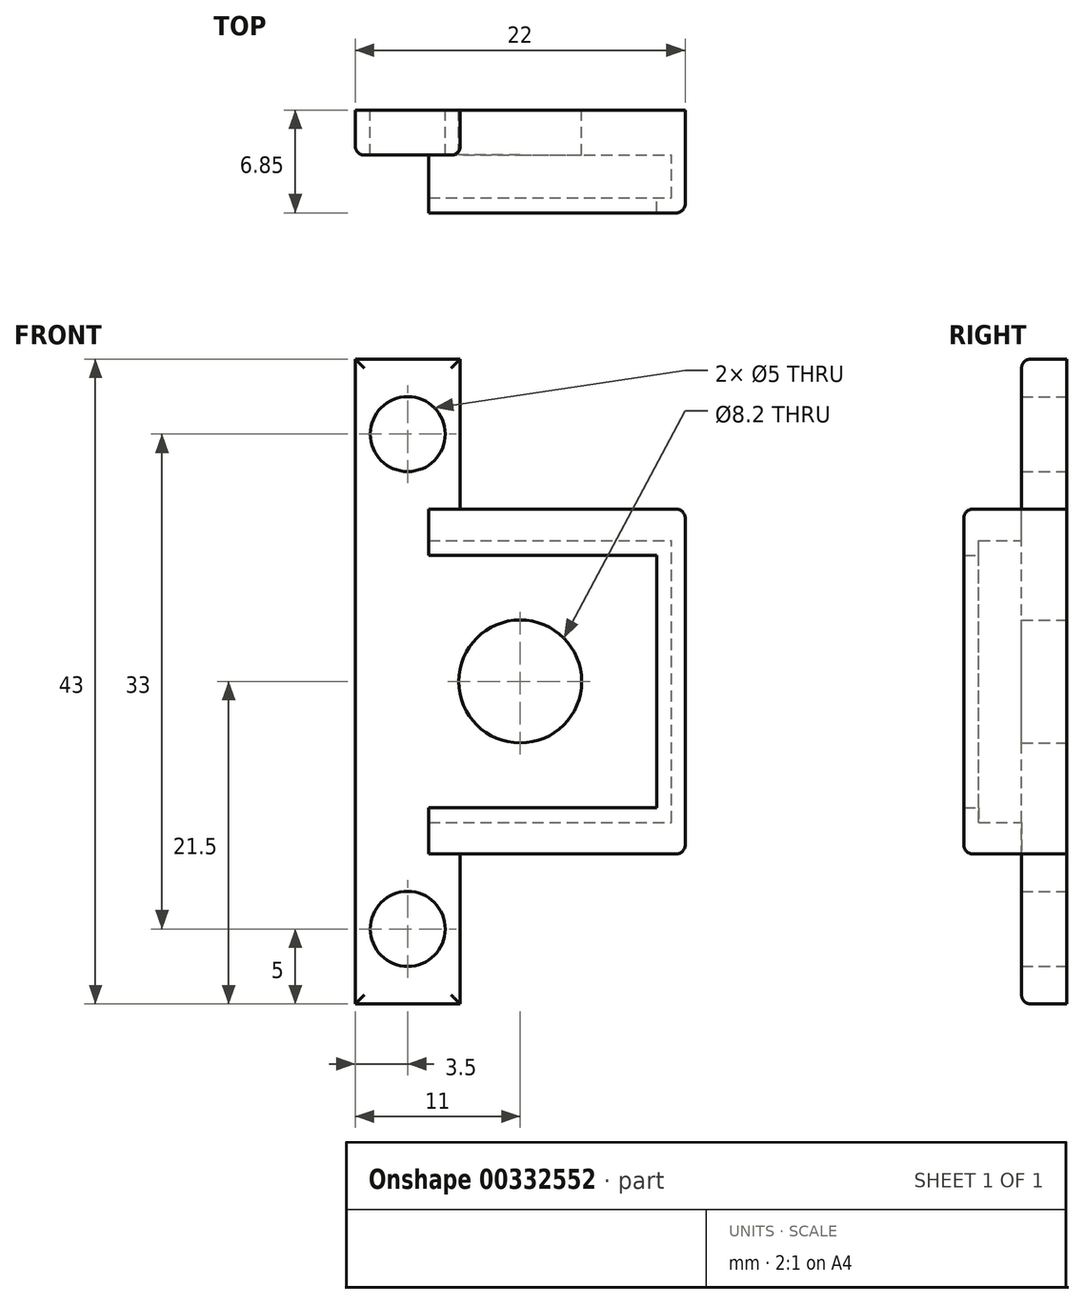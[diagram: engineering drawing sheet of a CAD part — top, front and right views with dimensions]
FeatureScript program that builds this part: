
annotation { "Feature Type Name" : "Feature", "Feature Type Description" : "" }
export const myFeature = defineFeature(function(context is Context, id is Id, definition is map)
    precondition{}
    {
        {
            var Q0;
            Q0=qCreatedBy(makeId("Front.planeOp"),FACE);
            var sketch = newSketch(context, id + "F0", { "sketchPlane" : qUnion([Q0])});
            skLineSegment(sketch, "E0.bottom", {"start": v(0, 0) * mm, "end": v(22, 0) * mm});
            skLineSegment(sketch, "E0.top", {"start": v(0, 23) * mm, "end": v(22, 23) * mm});
            skLineSegment(sketch, "E0.left", {"start": v(0, 0) * mm, "end": v(0, 23) * mm});
            skLineSegment(sketch, "E0.right", {"start": v(22, 0) * mm, "end": v(22, 23) * mm});
            skLineSegment(sketch, "E1.bottom", {"start": v(21.1, 20.9) * mm, "end": v(0.9, 20.9) * mm});
            skLineSegment(sketch, "E1.top", {"start": v(21.1, 2.1) * mm, "end": v(0.9, 2.1) * mm});
            skLineSegment(sketch, "E1.left", {"start": v(21.1, 20.9) * mm, "end": v(21.1, 2.1) * mm});
            skLineSegment(sketch, "E1.right", {"start": v(0.9, 20.9) * mm, "end": v(0.9, 2.1) * mm});
            skPoint(sketch, "E2", {"position": v(4.9, 20.9) * mm});
            skPoint(sketch, "E3", {"position": v(4.9, 2.1) * mm});
            skPoint(sketch, "E4", {"position": v(22, 1.5) * mm});
            skPoint(sketch, "E5", {"position": v(22, 21.5) * mm});
            skPoint(sketch, "E6", {"position": v(0, 1.5) * mm});
            skLineSegment(sketch, "E7.bottom", {"start": v(22, 0) * mm, "end": v(15, 0) * mm});
            skLineSegment(sketch, "E7.top", {"start": v(22, -10) * mm, "end": v(15, -10) * mm});
            skLineSegment(sketch, "E7.left", {"start": v(22, 0) * mm, "end": v(22, -10) * mm});
            skLineSegment(sketch, "E7.right", {"start": v(15, 0) * mm, "end": v(15, -10) * mm});
            skLineSegment(sketch, "E8.bottom", {"start": v(0, 0) * mm, "end": v(7, 0) * mm});
            skLineSegment(sketch, "E8.top", {"start": v(0, -10) * mm, "end": v(7, -10) * mm});
            skLineSegment(sketch, "E8.left", {"start": v(0, 0) * mm, "end": v(0, -10) * mm});
            skLineSegment(sketch, "E8.right", {"start": v(7, 0) * mm, "end": v(7, -10) * mm});
            skLineSegment(sketch, "E9.bottom", {"start": v(0, 23) * mm, "end": v(7, 23) * mm});
            skLineSegment(sketch, "E9.top", {"start": v(0, 33) * mm, "end": v(7, 33) * mm});
            skLineSegment(sketch, "E9.left", {"start": v(0, 23) * mm, "end": v(0, 33) * mm});
            skLineSegment(sketch, "E9.right", {"start": v(7, 23) * mm, "end": v(7, 33) * mm});
            skLineSegment(sketch, "E10.bottom", {"start": v(22, 23) * mm, "end": v(15, 23) * mm});
            skLineSegment(sketch, "E10.top", {"start": v(22, 33) * mm, "end": v(15, 33) * mm});
            skLineSegment(sketch, "E10.left", {"start": v(22, 23) * mm, "end": v(22, 33) * mm});
            skLineSegment(sketch, "E10.right", {"start": v(15, 23) * mm, "end": v(15, 33) * mm});
            skPoint(sketch, "E11", {"position": v(11, 11.5) * mm});
            skLineSegment(sketch, "E12", {"start": v(13.1, 11.9) * mm, "end": v(8.66, 7.89) * mm});
            skPoint(sketch, "E13", {"position": v(3.5, -5) * mm});
            skLineSegment(sketch, "E14", {"start": v(4.03, -4.24) * mm, "end": v(2.85, -5.92) * mm});
            skPoint(sketch, "E15", {"position": v(3.5, 28) * mm});
            skPoint(sketch, "E16", {"position": v(18.5, 28) * mm});
            skPoint(sketch, "E17", {"position": v(18.5, -5) * mm});
            skLineSegment(sketch, "E18", {"start": v(17.83, -4.05) * mm, "end": v(19.6, -6.56) * mm});
            skLineSegment(sketch, "E19", {"start": v(19.35, 26.22) * mm, "end": v(17.47, 23.53) * mm});
            skLineSegment(sketch, "E20", {"start": v(4.68, 23.31) * mm, "end": v(2.86, 25.9) * mm});
            skLineSegment(sketch, "E21", {"start": v(4.9, 20.9) * mm, "end": v(4.9, 23) * mm});
            skLineSegment(sketch, "E22", {"start": v(4.9, 2.1) * mm, "end": v(4.9, 0) * mm});
            skPoint(sketch, "E23", {"position": v(11, 20.9) * mm});
            skPoint(sketch, "E24", {"position": v(11, 2.1) * mm});
            skSolve(sketch);
        }
        {
            var Q0;
            Q0=makeQuery(id+"F0.imprint","IMPRINT",FACE,{"disambiguationData":[TD([[makeQuery(id+"F0.imprint","IMPRINT",EDGE,{"derivedFrom":sQuery(id+"F0.wireOp",EDGE,"E1.bottom")}),1.0]])]});
            var Q1;
            Q1=makeQuery(id+"F0.imprint","IMPRINT",FACE,{"disambiguationData":[TD([[makeQuery(id+"F0.imprint","IMPRINT",EDGE,{"derivedFrom":sQuery(id+"F0.wireOp",EDGE,"E0.bottom")}),1.0]])]});
            extrude(context, id + "F1", {"entities" : qUnion([Q0, Q1]), "depth" : 3 * mm});
        }
        {
            var Q0;
            {var subQ0=sQuery(id+"F0.wireOp",EDGE,"E0.right");Q0=makeQuery(id+"F0.imprint","IMPRINT",FACE,{"disambiguationData":[TD([[makeQuery(id+"F0.imprint","IMPRINT",EDGE,{"derivedFrom":subQ0}),1.0]])]});}
            extrude(context, id + "F2", {"entities" : qUnion([Q0]), "operationType" : NewBodyOperationType.ADD, "depth" : 6.85 * mm});
        }
        {
            var Q0;
            Q0=makeQuery(id+"F2.opExtrude","SWEPT_FACE",FACE,{"disambiguationData":[OSD([sQuery(id+"F0.wireOp",EDGE,"E1.bottom")])]});
            var sketch = newSketch(context, id + "F3", { "sketchPlane" : qUnion([Q0])});
            skLineSegment(sketch, "E25.bottom", {"start": v(21.1, 6.85) * mm, "end": v(21.1, 6.85) * mm});
            skLineSegment(sketch, "E25.top", {"start": v(21.1, 5.85) * mm, "end": v(21.1, 5.85) * mm});
            skLineSegment(sketch, "E25.left", {"start": v(21.1, 6.85) * mm, "end": v(21.1, 5.85) * mm});
            skLineSegment(sketch, "E25.right", {"start": v(21.1, 6.85) * mm, "end": v(21.1, 5.85) * mm});
            skLineSegment(sketch, "E26.bottom", {"start": v(4.9, 6.85) * mm, "end": v(21.1, 6.85) * mm});
            skLineSegment(sketch, "E26.top", {"start": v(4.9, 5.85) * mm, "end": v(21.1, 5.85) * mm});
            skLineSegment(sketch, "E26.left", {"start": v(4.9, 6.85) * mm, "end": v(4.9, 5.85) * mm});
            skSolve(sketch);
        }
        {
            var Q0;
            Q0=makeQuery(id+"F2.opExtrude","SWEPT_FACE",FACE,{"disambiguationData":[OSD([sQuery(id+"F0.wireOp",EDGE,"E1.left")])]});
            var sketch = newSketch(context, id + "F4", { "sketchPlane" : qUnion([Q0])});
            skLineSegment(sketch, "E27.bottom", {"start": v(6.85, 2.1) * mm, "end": v(5.85, 2.1) * mm});
            skLineSegment(sketch, "E27.top", {"start": v(6.85, 20.9) * mm, "end": v(5.85, 20.9) * mm});
            skLineSegment(sketch, "E27.left", {"start": v(6.85, 2.1) * mm, "end": v(6.85, 20.9) * mm});
            skLineSegment(sketch, "E27.right", {"start": v(5.85, 2.1) * mm, "end": v(5.85, 20.9) * mm});
            skSolve(sketch);
        }
        {
            var Q0;
            Q0=makeQuery(id+"F2.opExtrude","SWEPT_FACE",FACE,{"disambiguationData":[OSD([sQuery(id+"F0.wireOp",EDGE,"E1.top")])]});
            var sketch = newSketch(context, id + "F5", { "sketchPlane" : qUnion([Q0])});
            skLineSegment(sketch, "E28.bottom", {"start": v(21.1, -6.85) * mm, "end": v(21.1, -6.85) * mm});
            skLineSegment(sketch, "E28.top", {"start": v(21.1, -5.85) * mm, "end": v(21.1, -5.85) * mm});
            skLineSegment(sketch, "E28.left", {"start": v(21.1, -6.85) * mm, "end": v(21.1, -5.85) * mm});
            skLineSegment(sketch, "E28.right", {"start": v(21.1, -6.85) * mm, "end": v(21.1, -5.85) * mm});
            skLineSegment(sketch, "E29.bottom", {"start": v(4.9, -6.85) * mm, "end": v(21.1, -6.85) * mm});
            skLineSegment(sketch, "E29.top", {"start": v(4.9, -5.85) * mm, "end": v(21.1, -5.85) * mm});
            skLineSegment(sketch, "E29.left", {"start": v(4.9, -6.85) * mm, "end": v(4.9, -5.85) * mm});
            skSolve(sketch);
        }
        {
            var Q0;
            {var subQ4=sQuery(id+"F0.wireOp",EDGE,"E0.left");Q0=makeQuery(id+"F0.imprint","IMPRINT",FACE,{"disambiguationData":[TD([[makeQuery(id+"F0.imprint","IMPRINT",EDGE,{"derivedFrom":subQ4}),-1.0]])]});}
            extrude(context, id + "F6", {"entities" : qUnion([Q0]), "operationType" : NewBodyOperationType.ADD, "depth" : 3 * mm});
        }
        {
            var Q0;
            Q0=makeQuery(id+"F3.imprint","IMPRINT",FACE,{"disambiguationData":[TD([[makeQuery(id+"F3.imprint","IMPRINT",EDGE,{"derivedFrom":sQuery(id+"F3.wireOp",EDGE,"E25.bottom")}),1.0]])]});
            var Q1;
            Q1=makeQuery(id+"F3.imprint","IMPRINT",FACE,{"disambiguationData":[TD([[makeQuery(id+"F3.imprint","IMPRINT",EDGE,{"derivedFrom":sQuery(id+"F3.wireOp",EDGE,"E26.bottom")}),1.0]])]});
            extrude(context, id + "F7", {"entities" : qUnion([Q0, Q1]), "operationType" : NewBodyOperationType.ADD, "depth" : 1 * mm});
        }
        {
            var Q0;
            Q0=makeQuery(id+"F5.imprint","IMPRINT",FACE,{"disambiguationData":[TD([[makeQuery(id+"F5.imprint","IMPRINT",EDGE,{"derivedFrom":sQuery(id+"F5.wireOp",EDGE,"E28.bottom")}),-1.0]])]});
            var Q1;
            Q1=makeQuery(id+"F5.imprint","IMPRINT",FACE,{"disambiguationData":[TD([[makeQuery(id+"F5.imprint","IMPRINT",EDGE,{"derivedFrom":sQuery(id+"F5.wireOp",EDGE,"E29.bottom")}),-1.0]])]});
            extrude(context, id + "F8", {"entities" : qUnion([Q0, Q1]), "operationType" : NewBodyOperationType.ADD, "depth" : 1 * mm});
        }
        {
            var Q0;
            Q0=makeQuery(id+"F4.imprint","IMPRINT",FACE,{"disambiguationData":[TD([[makeQuery(id+"F4.imprint","IMPRINT",EDGE,{"derivedFrom":sQuery(id+"F4.wireOp",EDGE,"E27.bottom")}),-1.0]])]});
            extrude(context, id + "F9", {"entities" : qUnion([Q0]), "operationType" : NewBodyOperationType.ADD, "depth" : 1 * mm});
        }
        {
            var Q0;
            Q0=makeQuery(id+"F0.imprint","IMPRINT",FACE,{"disambiguationData":[TD([[makeQuery(id+"F0.imprint","IMPRINT",EDGE,{"derivedFrom":sQuery(id+"F0.wireOp",EDGE,"E10.bottom")}),-1.0]])]});
            var Q1;
            Q1=makeQuery(id+"F0.imprint","IMPRINT",FACE,{"disambiguationData":[TD([[makeQuery(id+"F0.imprint","IMPRINT",EDGE,{"derivedFrom":sQuery(id+"F0.wireOp",EDGE,"E7.bottom")}),1.0]])]});
            var Q2;
            Q2=makeQuery(id+"F0.imprint","IMPRINT",FACE,{"disambiguationData":[TD([[makeQuery(id+"F0.imprint","IMPRINT",EDGE,{"derivedFrom":sQuery(id+"F0.wireOp",EDGE,"E9.top")}),-1.0]])]});
            var Q3;
            Q3=makeQuery(id+"F0.imprint","IMPRINT",FACE,{"disambiguationData":[TD([[makeQuery(id+"F0.imprint","IMPRINT",EDGE,{"derivedFrom":sQuery(id+"F0.wireOp",EDGE,"E8.top")}),1.0]])]});
            extrude(context, id + "F10", {"entities" : qUnion([Q0, Q1, Q2, Q3]), "operationType" : NewBodyOperationType.ADD, "depth" : 3 * mm});
        }
        {
            var Q0;
            Q0=sQuery(id+"F0.wireOp",VERTEX,"E11");
            var Q1;
            Q1=makeQuery(id+"F1.opExtrude","SWEPT_BODY",BODY,{"disambiguationData":[OSD([sQuery(id+"F0.wireOp",EDGE,"E0.bottom"),sQuery(id+"F0.wireOp",EDGE,"E0.top"),sQuery(id+"F0.wireOp",EDGE,"E0.right"),sQuery(id+"F0.wireOp",EDGE,"E1.bottom"),sQuery(id+"F0.wireOp",EDGE,"E1.top"),sQuery(id+"F0.wireOp",EDGE,"E1.right"),sQuery(id+"F0.wireOp",EDGE,"IjJQbh8V-s165-LqST-yhQQ-smVxdiDUJUNB"),sQuery(id+"F0.wireOp",EDGE,"vMIWCNPO-odwN-dmoI-aRjE-b61Hn6vikTsy"),sQuery(id+"F0.wireOp",EDGE,"E7.bottom"),sQuery(id+"F0.wireOp",EDGE,"E8.bottom"),sQuery(id+"F0.wireOp",EDGE,"E9.bottom"),sQuery(id+"F0.wireOp",EDGE,"E10.bottom")])]});
            hole(context, id + "F11", {"style" : HoleStyle.SIMPLE, "endStyle" : HoleEndStyle.THROUGH, "oppositeDirection" : true, "holeDiameter" : 8.2 * mm, "tappedDepth" : 12 * mm, "tapClearance" : 3, "locations" : qUnion([Q0]), "scope" : qUnion([Q1])});
        }
        {
            var Q0;
            Q0=sQuery(id+"F0.wireOp",VERTEX,"E15");
            var Q1;
            Q1=sQuery(id+"F0.wireOp",VERTEX,"E16");
            var Q2;
            Q2=sQuery(id+"F0.wireOp",VERTEX,"E13");
            var Q3;
            Q3=sQuery(id+"F0.wireOp",VERTEX,"E17");
            var Q4;
            Q4=makeQuery(id+"F1.opExtrude","SWEPT_BODY",BODY,{"disambiguationData":[OSD([sQuery(id+"F0.wireOp",EDGE,"E0.bottom"),sQuery(id+"F0.wireOp",EDGE,"E0.top"),sQuery(id+"F0.wireOp",EDGE,"E0.right"),sQuery(id+"F0.wireOp",EDGE,"E1.bottom"),sQuery(id+"F0.wireOp",EDGE,"E1.top"),sQuery(id+"F0.wireOp",EDGE,"E1.right"),sQuery(id+"F0.wireOp",EDGE,"IjJQbh8V-s165-LqST-yhQQ-smVxdiDUJUNB"),sQuery(id+"F0.wireOp",EDGE,"vMIWCNPO-odwN-dmoI-aRjE-b61Hn6vikTsy"),sQuery(id+"F0.wireOp",EDGE,"E7.bottom"),sQuery(id+"F0.wireOp",EDGE,"E8.bottom"),sQuery(id+"F0.wireOp",EDGE,"E9.bottom"),sQuery(id+"F0.wireOp",EDGE,"E10.bottom")])]});
            hole(context, id + "F12", {"style" : HoleStyle.SIMPLE, "endStyle" : HoleEndStyle.THROUGH, "oppositeDirection" : true, "holeDiameter" : 5 * mm, "tappedDepth" : 12 * mm, "tapClearance" : 3, "locations" : qUnion([Q0, Q1, Q2, Q3]), "scope" : qUnion([Q4])});
        }
        {
            var Q0;
            Q0=makeQuery(id+"F10.boolean.opBoolean","MERGE",EDGE,{"derivedFrom":[makeQuery(id+"F6.opExtrude","CAP_EDGE",EDGE,{"disambiguationData":[OSD([sQuery(id+"F0.wireOp",EDGE,"E0.left")])],"isStart":false}),makeQuery(id+"F10.opExtrude","CAP_EDGE",EDGE,{"disambiguationData":[OSD([sQuery(id+"F0.wireOp",EDGE,"E8.left")])],"isStart":false}),makeQuery(id+"F10.opExtrude","CAP_EDGE",EDGE,{"disambiguationData":[OSD([sQuery(id+"F0.wireOp",EDGE,"E9.left")])],"isStart":false})]});
            var Q1;
            Q1=makeQuery(id+"F10.opExtrude","CAP_EDGE",EDGE,{"disambiguationData":[OSD([sQuery(id+"F0.wireOp",EDGE,"E8.top")])],"isStart":false});
            var Q2;
            Q2=makeQuery(id+"F10.opExtrude","CAP_EDGE",EDGE,{"disambiguationData":[OSD([sQuery(id+"F0.wireOp",EDGE,"E8.right")])],"isStart":false});
            var Q3;
            Q3=makeQuery(id+"F10.opExtrude","CAP_EDGE",EDGE,{"disambiguationData":[OSD([sQuery(id+"F0.wireOp",EDGE,"E9.top")])],"isStart":false});
            var Q4;
            Q4=makeQuery(id+"F10.opExtrude","CAP_EDGE",EDGE,{"disambiguationData":[OSD([sQuery(id+"F0.wireOp",EDGE,"E9.right")])],"isStart":false});
            fillet(context, id + "F13", {"entities" : qUnion([Q0, Q1, Q2, Q3, Q4]), "radius" : 0.6 * mm, "tangentPropagation" : true, "allowEdgeOverflow" : false});
        }
        {
            var Q0;
            Q0=makeQuery(id+"F10.opExtrude","CAP_EDGE",EDGE,{"disambiguationData":[OSD([sQuery(id+"F0.wireOp",EDGE,"E7.left")])],"isStart":false});
            var Q1;
            Q1=makeQuery(id+"F10.opExtrude","CAP_EDGE",EDGE,{"disambiguationData":[OSD([sQuery(id+"F0.wireOp",EDGE,"E7.top")])],"isStart":false});
            var Q2;
            Q2=makeQuery(id+"F10.opExtrude","CAP_EDGE",EDGE,{"disambiguationData":[OSD([sQuery(id+"F0.wireOp",EDGE,"E7.right")])],"isStart":false});
            var Q3;
            {var subQ0=sQuery(id+"F0.wireOp",EDGE,"E7.left");var subQ1=sQuery(id+"F0.wireOp",EDGE,"E7.bottom");var subQ2=sQuery(id+"F0.wireOp",EDGE,"E0.right");Q3=makeQuery(id+"F2.boolean.opBoolean","MERGE",EDGE,{"derivedFrom":[makeQuery(id+"F1.opExtrude","SWEPT_EDGE",EDGE,{"disambiguationData":[OSD([subQ2,subQ1,subQ0])]}),makeQuery(id+"F2.opExtrude","SWEPT_EDGE",EDGE,{"disambiguationData":[OSD([subQ2,subQ1,subQ0])]})]});}
            var Q4;
            Q4=makeQuery(id+"F2.opExtrude","CAP_EDGE",EDGE,{"disambiguationData":[OSD([sQuery(id+"F0.wireOp",EDGE,"E0.right")])],"isStart":false});
            var Q5;
            {var subQ0=sQuery(id+"F0.wireOp",EDGE,"E10.left");var subQ1=sQuery(id+"F0.wireOp",EDGE,"E10.bottom");var subQ2=sQuery(id+"F0.wireOp",EDGE,"E0.right");Q5=makeQuery(id+"F2.boolean.opBoolean","MERGE",EDGE,{"derivedFrom":[makeQuery(id+"F1.opExtrude","SWEPT_EDGE",EDGE,{"disambiguationData":[OSD([subQ2,subQ1,subQ0])]}),makeQuery(id+"F2.opExtrude","SWEPT_EDGE",EDGE,{"disambiguationData":[OSD([subQ2,subQ1,subQ0])]})]});}
            var Q6;
            Q6=makeQuery(id+"F10.opExtrude","CAP_EDGE",EDGE,{"disambiguationData":[OSD([sQuery(id+"F0.wireOp",EDGE,"E10.left")])],"isStart":false});
            var Q7;
            Q7=makeQuery(id+"F10.opExtrude","CAP_EDGE",EDGE,{"disambiguationData":[OSD([sQuery(id+"F0.wireOp",EDGE,"E10.right")])],"isStart":false});
            var Q8;
            Q8=makeQuery(id+"F10.opExtrude","CAP_EDGE",EDGE,{"disambiguationData":[OSD([sQuery(id+"F0.wireOp",EDGE,"E10.top")])],"isStart":false});
            fillet(context, id + "F14", {"entities" : qUnion([Q0, Q1, Q2, Q3, Q4, Q5, Q6, Q7, Q8]), "radius" : 0.6 * mm, "tangentPropagation" : true, "allowEdgeOverflow" : false});
        }
        {
            var Q0;
            Q0=makeQuery(id+"F2.opExtrude","CAP_EDGE",EDGE,{"disambiguationData":[OSD([sQuery(id+"F0.wireOp",EDGE,"E0.top"),sQuery(id+"F0.wireOp",EDGE,"E9.bottom"),sQuery(id+"F0.wireOp",EDGE,"E10.bottom")])],"isStart":false});
            var Q1;
            Q1=makeQuery(id+"F2.opExtrude","CAP_EDGE",EDGE,{"disambiguationData":[OSD([sQuery(id+"F0.wireOp",EDGE,"E0.bottom"),sQuery(id+"F0.wireOp",EDGE,"E7.bottom"),sQuery(id+"F0.wireOp",EDGE,"E8.bottom")])],"isStart":false});
            fillet(context, id + "F15", {"entities" : qUnion([Q0, Q1]), "radius" : 0.6 * mm, "tangentPropagation" : true, "allowEdgeOverflow" : false});
        }
    });
